# Revit family: IEK_Выключатель_Встраиваемый_10А одноклавишный IP20_ВЕГА
name_source: partatom
category: Выключатели
units: mm (PartAtom-declared; Revit-internal decimal feet)

## family parameters
Всегда вертикально = Да
На основе рабочей плоскости = Нет
Общий = Нет
При загрузке вырезать с полостями = Нет
Размер круглого соединителя = Использовать диаметр
Сохранять ориентацию аннотаций = Да
Тип детали = Переключатель
Точка расчета площади = Нет

## types (2) — shared parameters
ADSK_URL страницы изделия = https://www.iek.ru
ADSK_Версия Revit = 2019
ADSK_Версия семейства = 1.0
ADSK_Группирование = III ЭЛЕКТРОУСТАНОВОЧНЫЕ И ЭЛЕКТРОМОНТАЖНЫЕ ИЗДЕЛИЯ
ADSK_Единица измерения = шт
ADSK_Завод-изготовитель = IEK
ADSK_Количество фаз = 1
ADSK_Количество фаз числовое = 1
ADSK_Марка = ВЕГА
ADSK_Материал = Цвет белый
ADSK_Материал наименование = Пластик
ADSK_Напряжение = 220 В
IEK_URL = https://www.iek.ru
IEK_Описание = Серия «ВЕГА» включает в себя розетки и выключатели для скрытого монтажа, которые хорошо впишутся в любой интерьер квартир, загородных домов, офисных и производственных помещений.
KSI_CMa_Строительные материалы = 01.7.14.03
KSI_CPr_Строительные изделия = 20.4.01
Высота = 81 мм
Глубина = 36 мм
Изготовитель = IEK
Степень защиты = IP20
Тип монтажа = Скрытый монтаж (в штукатурку)
Ширина = 82 мм

## per-type parameters (varying)
| type | ADSK_Код изделия | ADSK_Масса | ADSK_Наименование | IEK_Цена за единицу |
| ВС10-1-0-ВБ | EVV10-K01-10-DM | 0.065 | Выключатель 1-клавишный ВС10-1-0-ВБ 10А ВЕГА белый IEK | 93.42 |
| ВСп10-1-0-ВБ | EVV12-K01-10-DM | 0.058 | Выключатель 1-клавишный проходной ВСп10-1-0-ВБ 10А ВЕГА белый IEK | 117.85 |
